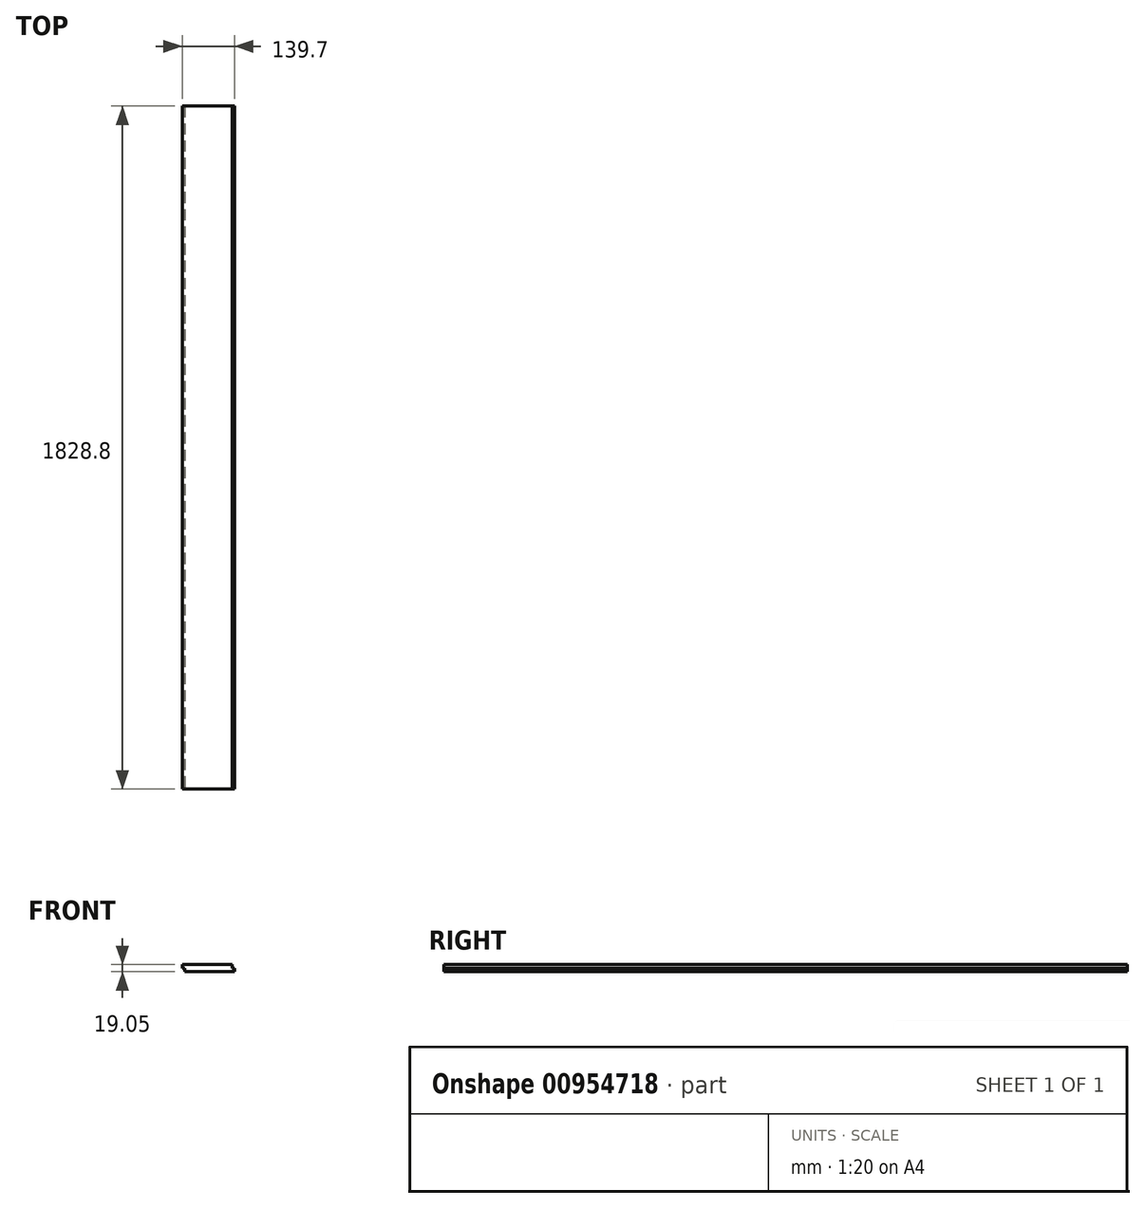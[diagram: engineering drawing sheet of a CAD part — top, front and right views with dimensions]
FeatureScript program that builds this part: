
annotation { "Feature Type Name" : "Feature", "Feature Type Description" : "" }
export const myFeature = defineFeature(function(context is Context, id is Id, definition is map)
    precondition{}
    {
        {
            var Q0;
            Q0=qCreatedBy(makeId("Front.planeOp"),FACE);
            var sketch = newSketch(context, id + "F0", { "sketchPlane" : qUnion([Q0])});
            skLineSegment(sketch, "E0.bottom", {"start": v(0, 0) * mm, "end": v(139.7, 0) * mm});
            skLineSegment(sketch, "E0.top", {"start": v(0, 19.05) * mm, "end": v(139.7, 19.05) * mm});
            skLineSegment(sketch, "E0.left", {"start": v(0, 0) * mm, "end": v(0, 19.05) * mm});
            skLineSegment(sketch, "E0.right", {"start": v(139.7, 0) * mm, "end": v(139.7, 19.05) * mm});
            skSolve(sketch);
        }
        {
            var Q0;
            Q0 = qSketchRegion(id + "F0", true);
            extrude(context, id + "F1", {"entities" : qUnion([Q0]), "depth" : 1828.8 * mm, "offsetDistance" : 25.4 * mm});
        }
        {
            var Q0;
            Q0=makeQuery(id+"F1.opExtrude","CAP_FACE",FACE,{"disambiguationData":[OSD([sQuery(id+"F0.wireOp",EDGE,"E0.bottom"),sQuery(id+"F0.wireOp",EDGE,"E0.top"),sQuery(id+"F0.wireOp",EDGE,"E0.left"),sQuery(id+"F0.wireOp",EDGE,"E0.right")])],"isStart":false});
            var sketch = newSketch(context, id + "F2", { "sketchPlane" : qUnion([Q0])});
            skPoint(sketch, "E1.oppositeSnap0", {"position": v(0, 9.53) * mm});
            skLineSegment(sketch, "E1.bottom", {"start": v(0, 0) * mm, "end": v(6.35, 0) * mm});
            skLineSegment(sketch, "E1.top", {"start": v(0, 9.53) * mm, "end": v(6.35, 9.53) * mm});
            skLineSegment(sketch, "E1.left", {"start": v(0, 0) * mm, "end": v(0, 9.53) * mm});
            skLineSegment(sketch, "E1.right", {"start": v(6.35, 0) * mm, "end": v(6.35, 9.53) * mm});
            skLineSegment(sketch, "E2.bottom", {"start": v(139.7, 19.05) * mm, "end": v(133.35, 19.05) * mm});
            skLineSegment(sketch, "E2.top", {"start": v(139.7, 9.53) * mm, "end": v(133.35, 9.53) * mm});
            skLineSegment(sketch, "E2.left", {"start": v(139.7, 19.05) * mm, "end": v(139.7, 9.53) * mm});
            skLineSegment(sketch, "E2.right", {"start": v(133.35, 19.05) * mm, "end": v(133.35, 9.53) * mm});
            skSolve(sketch);
        }
        {
            var Q0;
            Q0 = qSketchRegion(id + "F2", true);
            extrude(context, id + "F3", {"entities" : qUnion([Q0]), "operationType" : NewBodyOperationType.REMOVE, "endBound" : BoundingType.THROUGH_ALL, "oppositeDirection" : true, "depth" : 25.4 * mm, "offsetDistance" : 25.4 * mm});
        }
    });
